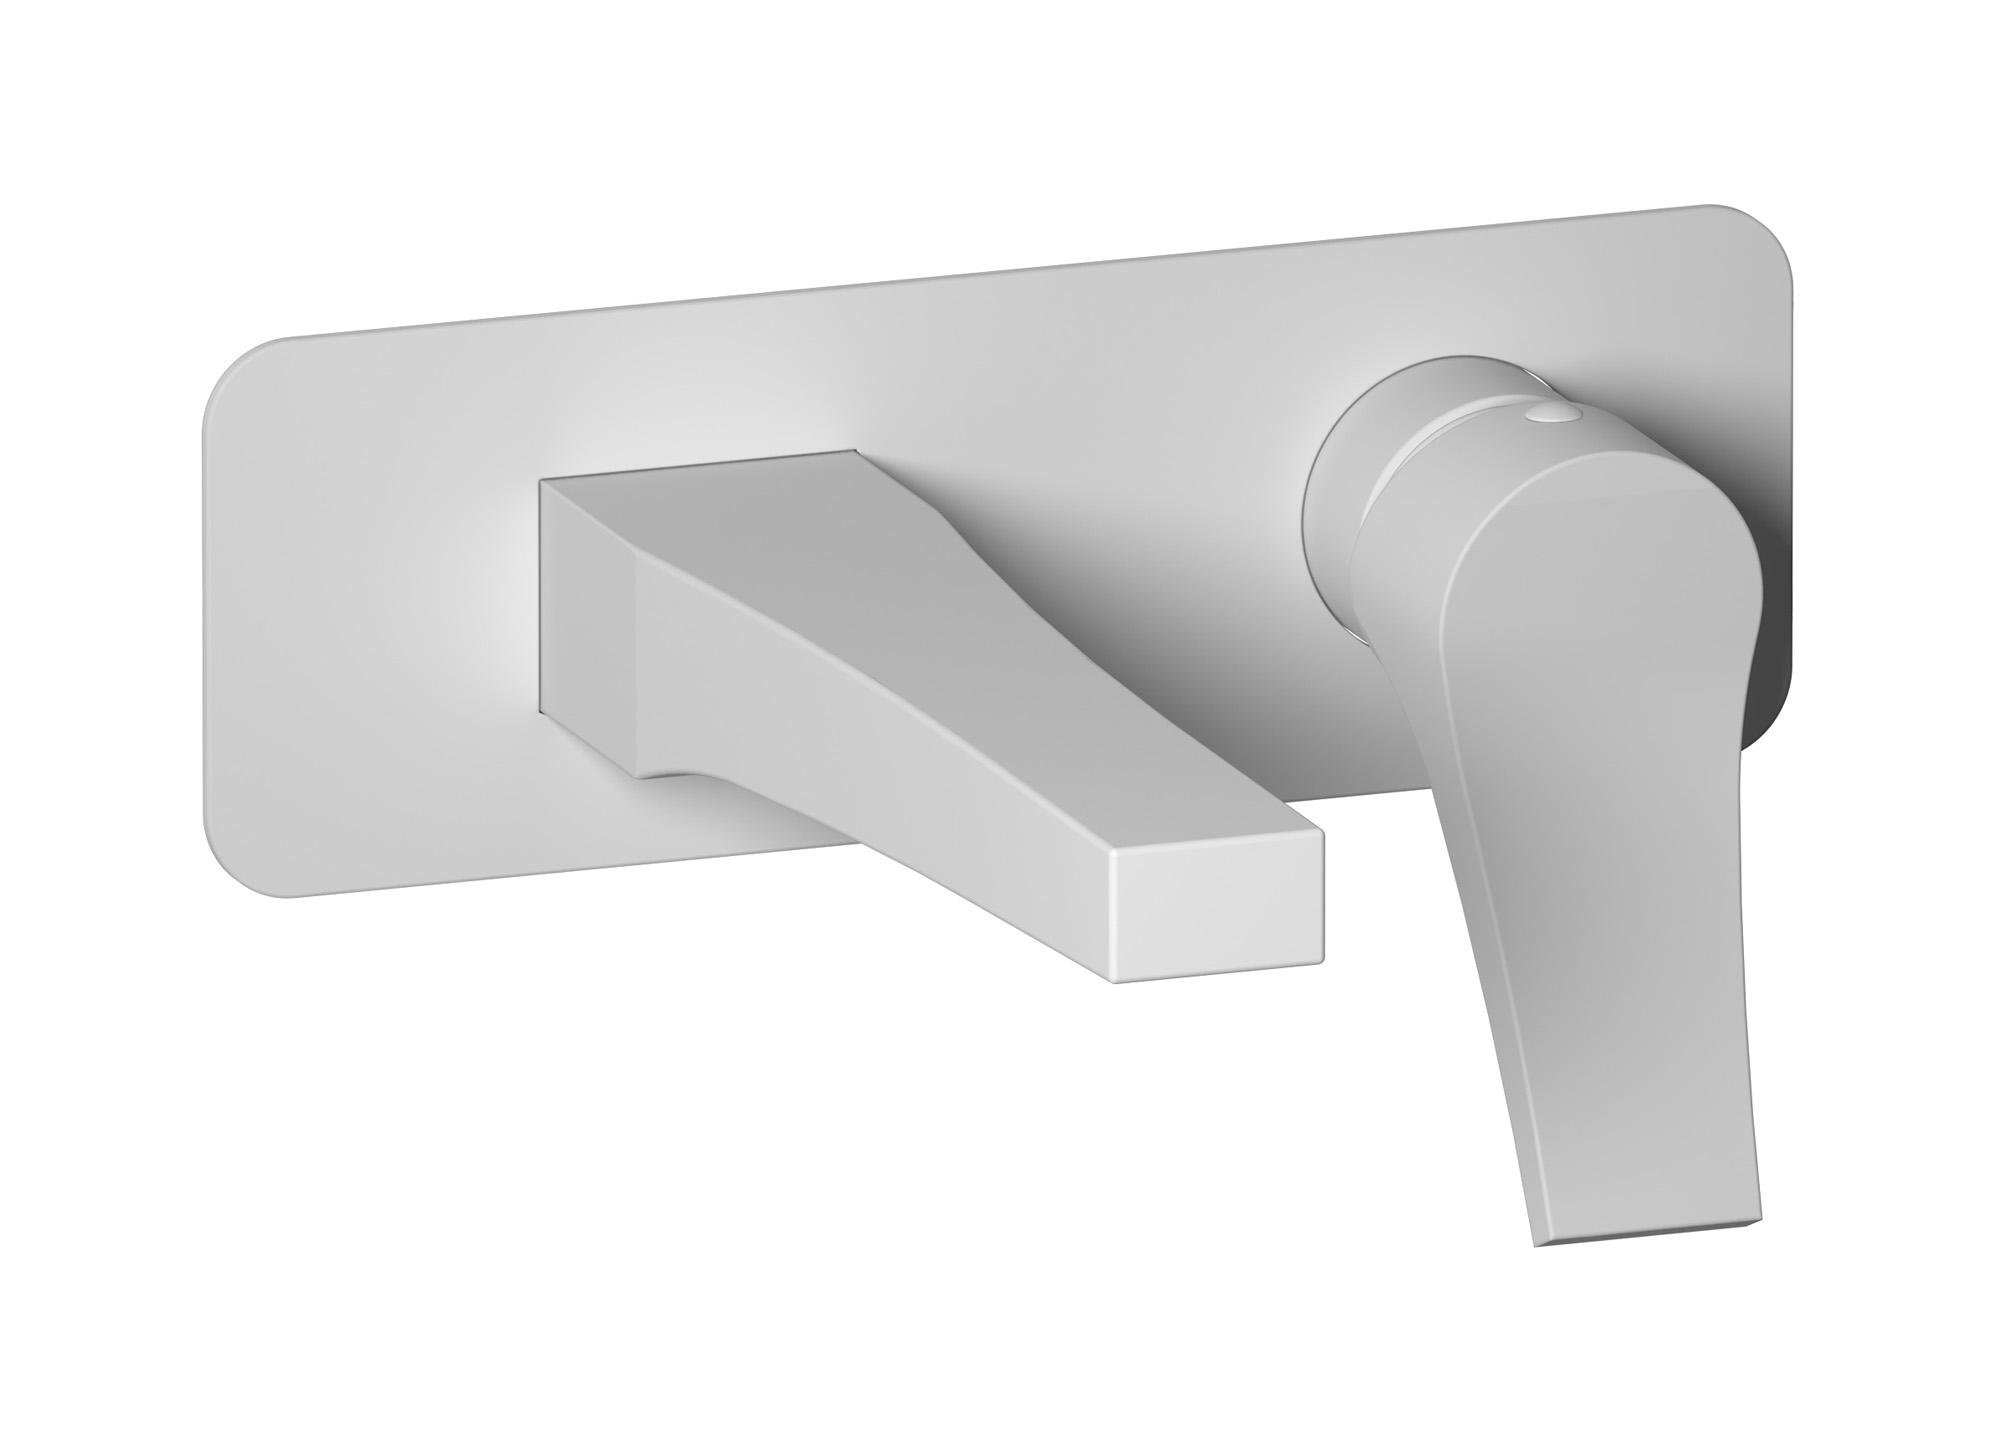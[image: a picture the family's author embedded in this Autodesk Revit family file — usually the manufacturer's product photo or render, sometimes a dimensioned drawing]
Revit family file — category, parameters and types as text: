
# Revit family: TW206
name_source: partatom
category: Apparecchi idraulici
units: mm (PartAtom-declared; Revit-internal decimal feet)

## family parameters
Basato su piano di lavoro = No
Condiviso = No
Mantieni orientamento annotazione = No
Numero OmniClass = 23.45.55.17
Punto di calcolo locali = No
Quota connettore circolare = Usa diametro
Sempre verticale = Sì
Taglio con vuoti quando caricato = No
Tipo di parte = Normale
Titolo OmniClass = Mixing Faucets

## types (12) — shared parameters
Cold water inlet = 10 mm  [stored 0.0328084 ft]
Commenti sul tipo = Washbasin mixer
Connessione CW = No
Connessione HW = No
Connessione di scarico = No
Connessione di ventilazione = No
Descrizione = Wall mounted washbasin mixer complete with drain
Hot water inlet = 10 mm  [stored 0.0328084 ft]
Produttore = IB Rubinetterie S.p.A.
URL = https://www.weareib.it
zero-valued in all types: Prospetto di default

## per-type parameters (varying)
| type | Finishes surface | Immagine tipo | Modello |
| Chrome | IB_Chrome | TW206CC.jpg | TW206CC |
| Brushed nickel | IB_Brushed nickel | TW206SS.jpg | TW206SS |
| Matt black | IB_matt black | TW206NP.jpg | TW206NP |
| Matt white | IB_matt white | TW206BO.jpg | TW206BO |
| Black chrome | IB_Black chrome | TW206CF.jpg | TW206CF |
| Brushed black chrome | IB_Brushed black chrome | TW206CS.jpg | TW206CS |
| Pale gold | IB_Pale gold | TW206II.jpg | TW206II |
| Brushed pale gold | IB_brushed pale gold | TW206IS.jpg | TW206IS |
| Rose gold | IB_Rose gold | TW206RS.jpg | TW206RS |
| Brushed rose gold | IB_Brushed rose gold | TW206SR.jpg | TW206SR |
| Gold | IB_gold | TW206OO.jpg | TW206OO |
| Brushed gold | IB_brushed gold | TW206OS.jpg | TW206OS |

note: [stored X ft] marks values corroborated as IEEE doubles in the binary element streams (Revit-internal decimal feet)
